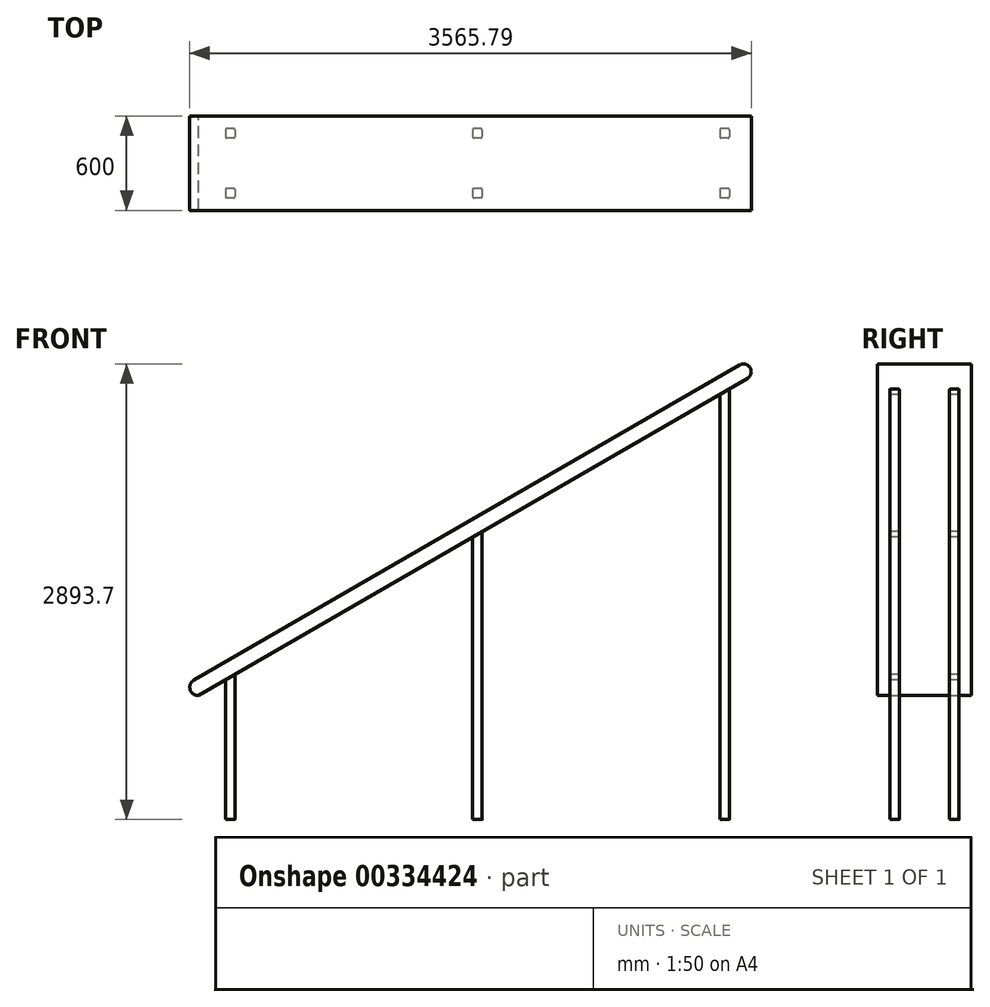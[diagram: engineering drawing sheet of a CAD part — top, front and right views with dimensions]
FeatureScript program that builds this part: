
annotation { "Feature Type Name" : "Feature", "Feature Type Description" : "" }
export const myFeature = defineFeature(function(context is Context, id is Id, definition is map)
    precondition{}
    {
        {
            var Q0;
            Q0=qCreatedBy(makeId("Front.planeOp"),FACE);
            var sketch = newSketch(context, id + "F0", { "sketchPlane" : qUnion([Q0])});
            skLineSegment(sketch, "E0.bottom", {"start": v(-3436.6, -2099.6) * mm, "end": v(50, -86.6) * mm});
            skLineSegment(sketch, "E0.top", {"start": v(-3464.1, -2000) * mm, "end": v(0, 0) * mm});
            skArc(sketch, "E1", {"start": v(-3464.1, -2000) * mm, "mid": v(-3488.86, -2060.43) * mm, "end": v(-3436.6, -2099.6) * mm});
            skArc(sketch, "E2", {"start": v(50, -86.6) * mm, "mid": v(68.3, -18.3) * mm, "end": v(0, 0) * mm});
            skLineSegment(sketch, "E3", {"start": v(25, -43.3) * mm, "end": v(-1405.55, -43.3) * mm, "construction": true});
            skSolve(sketch);
        }
        {
            var Q0;
            Q0 = qSketchRegion(id + "F0", true);
            extrude(context, id + "F1", {"entities" : qUnion([Q0]), "depth" : 600 * mm});
        }
        {
            var Q0;
            Q0=qCreatedBy(makeId("Top.planeOp"),FACE);
            cPlane(context, id + "F2", {"entities" : qUnion([Q0]), "cplaneType" : CPlaneType.OFFSET, "offset" : 2887 * mm, "oppositeDirection" : true, "width" : 150 * mm, "height" : 150 * mm});
        }
        {
            var Q0;
            Q0=qCreatedBy(id+"F2.planeOp",FACE);
            var sketch = newSketch(context, id + "F3", { "sketchPlane" : qUnion([Q0])});
            skLineSegment(sketch, "E4.bottom", {"start": v(-3212.1, -80) * mm, "end": v(-3256.1, -80) * mm});
            skLineSegment(sketch, "E4.top", {"start": v(-3212.1, -140) * mm, "end": v(-3256.1, -140) * mm});
            skLineSegment(sketch, "E4.left", {"start": v(-3204.1, -88) * mm, "end": v(-3204.1, -132) * mm});
            skLineSegment(sketch, "E4.right", {"start": v(-3264.1, -88) * mm, "end": v(-3264.1, -132) * mm});
            skPoint(sketch, "E4.middle", {"position": v(-3234.1, -110) * mm});
            skPoint(sketch, "E5.visualSharp", {"position": v(-3264.1, -140) * mm});
            skArc(sketch, "E5.filletArc", {"start": v(-3264.1, -132) * mm, "mid": v(-3261.76, -137.66) * mm, "end": v(-3256.1, -140) * mm});
            skPoint(sketch, "E6.visualSharp", {"position": v(-3204.1, -140) * mm});
            skArc(sketch, "E6.filletArc", {"start": v(-3212.1, -140) * mm, "mid": v(-3206.44, -137.66) * mm, "end": v(-3204.1, -132) * mm});
            skPoint(sketch, "E7.visualSharp", {"position": v(-3204.1, -80) * mm});
            skArc(sketch, "E7.filletArc", {"start": v(-3204.1, -88) * mm, "mid": v(-3206.44, -82.34) * mm, "end": v(-3212.1, -80) * mm});
            skPoint(sketch, "E8.visualSharp", {"position": v(-3264.1, -80) * mm});
            skArc(sketch, "E8.filletArc", {"start": v(-3256.1, -80) * mm, "mid": v(-3261.76, -82.34) * mm, "end": v(-3264.1, -88) * mm});
            skLineSegment(sketch, "E9", {"start": v(-3745.7, -300) * mm, "end": v(99.52, -300) * mm, "construction": true});
            skPoint(sketch, "E10.0.1.0", {"position": v(-3204.1, -460) * mm});
            skPoint(sketch, "E10.0.1.1", {"position": v(-3264.1, -460) * mm});
            skLineSegment(sketch, "E10.0.1.2", {"start": v(-3212.1, -460) * mm, "end": v(-3256.1, -460) * mm});
            skPoint(sketch, "E10.0.1.3", {"position": v(-3204.1, -520) * mm});
            skLineSegment(sketch, "E10.0.1.4", {"start": v(-3264.1, -468) * mm, "end": v(-3264.1, -512) * mm});
            skLineSegment(sketch, "E10.0.1.5", {"start": v(-3204.1, -468) * mm, "end": v(-3204.1, -512) * mm});
            skLineSegment(sketch, "E10.0.1.6", {"start": v(-3212.1, -520) * mm, "end": v(-3256.1, -520) * mm});
            skPoint(sketch, "E10.0.1.7", {"position": v(-3234.1, -490) * mm});
            skPoint(sketch, "E10.0.1.8", {"position": v(-3264.1, -520) * mm});
            skArc(sketch, "E10.0.1.9", {"start": v(-3204.1, -468) * mm, "mid": v(-3206.44, -462.34) * mm, "end": v(-3212.1, -460) * mm});
            skArc(sketch, "E10.0.1.10", {"start": v(-3256.1, -460) * mm, "mid": v(-3261.76, -462.34) * mm, "end": v(-3264.1, -468) * mm});
            skArc(sketch, "E10.0.1.11", {"start": v(-3264.1, -512) * mm, "mid": v(-3261.76, -517.66) * mm, "end": v(-3256.1, -520) * mm});
            skArc(sketch, "E10.0.1.12", {"start": v(-3212.1, -520) * mm, "mid": v(-3206.44, -517.66) * mm, "end": v(-3204.1, -512) * mm});
            skPoint(sketch, "E10.1.0.0", {"position": v(-1634.1, -80) * mm});
            skPoint(sketch, "E10.1.0.1", {"position": v(-1694.1, -80) * mm});
            skLineSegment(sketch, "E10.1.0.2", {"start": v(-1642.1, -80) * mm, "end": v(-1686.1, -80) * mm});
            skPoint(sketch, "E10.1.0.3", {"position": v(-1634.1, -140) * mm});
            skLineSegment(sketch, "E10.1.0.4", {"start": v(-1694.1, -88) * mm, "end": v(-1694.1, -132) * mm});
            skLineSegment(sketch, "E10.1.0.5", {"start": v(-1634.1, -88) * mm, "end": v(-1634.1, -132) * mm});
            skLineSegment(sketch, "E10.1.0.6", {"start": v(-1642.1, -140) * mm, "end": v(-1686.1, -140) * mm});
            skPoint(sketch, "E10.1.0.7", {"position": v(-1664.1, -110) * mm});
            skPoint(sketch, "E10.1.0.8", {"position": v(-1694.1, -140) * mm});
            skArc(sketch, "E10.1.0.9", {"start": v(-1634.1, -88) * mm, "mid": v(-1636.44, -82.34) * mm, "end": v(-1642.1, -80) * mm});
            skArc(sketch, "E10.1.0.10", {"start": v(-1686.1, -80) * mm, "mid": v(-1691.76, -82.34) * mm, "end": v(-1694.1, -88) * mm});
            skArc(sketch, "E10.1.0.11", {"start": v(-1694.1, -132) * mm, "mid": v(-1691.76, -137.66) * mm, "end": v(-1686.1, -140) * mm});
            skArc(sketch, "E10.1.0.12", {"start": v(-1642.1, -140) * mm, "mid": v(-1636.44, -137.66) * mm, "end": v(-1634.1, -132) * mm});
            skPoint(sketch, "E10.1.1.0", {"position": v(-1634.1, -460) * mm});
            skPoint(sketch, "E10.1.1.1", {"position": v(-1694.1, -460) * mm});
            skLineSegment(sketch, "E10.1.1.2", {"start": v(-1642.1, -460) * mm, "end": v(-1686.1, -460) * mm});
            skPoint(sketch, "E10.1.1.3", {"position": v(-1634.1, -520) * mm});
            skLineSegment(sketch, "E10.1.1.4", {"start": v(-1694.1, -468) * mm, "end": v(-1694.1, -512) * mm});
            skLineSegment(sketch, "E10.1.1.5", {"start": v(-1634.1, -468) * mm, "end": v(-1634.1, -512) * mm});
            skLineSegment(sketch, "E10.1.1.6", {"start": v(-1642.1, -520) * mm, "end": v(-1686.1, -520) * mm});
            skPoint(sketch, "E10.1.1.7", {"position": v(-1664.1, -490) * mm});
            skPoint(sketch, "E10.1.1.8", {"position": v(-1694.1, -520) * mm});
            skArc(sketch, "E10.1.1.9", {"start": v(-1634.1, -468) * mm, "mid": v(-1636.44, -462.34) * mm, "end": v(-1642.1, -460) * mm});
            skArc(sketch, "E10.1.1.10", {"start": v(-1686.1, -460) * mm, "mid": v(-1691.76, -462.34) * mm, "end": v(-1694.1, -468) * mm});
            skArc(sketch, "E10.1.1.11", {"start": v(-1694.1, -512) * mm, "mid": v(-1691.76, -517.66) * mm, "end": v(-1686.1, -520) * mm});
            skArc(sketch, "E10.1.1.12", {"start": v(-1642.1, -520) * mm, "mid": v(-1636.44, -517.66) * mm, "end": v(-1634.1, -512) * mm});
            skPoint(sketch, "E10.2.0.0", {"position": v(-64.1, -80) * mm});
            skPoint(sketch, "E10.2.0.1", {"position": v(-124.1, -80) * mm});
            skLineSegment(sketch, "E10.2.0.2", {"start": v(-72.1, -80) * mm, "end": v(-116.1, -80) * mm});
            skPoint(sketch, "E10.2.0.3", {"position": v(-64.1, -140) * mm});
            skLineSegment(sketch, "E10.2.0.4", {"start": v(-124.1, -88) * mm, "end": v(-124.1, -132) * mm});
            skLineSegment(sketch, "E10.2.0.5", {"start": v(-64.1, -88) * mm, "end": v(-64.1, -132) * mm});
            skLineSegment(sketch, "E10.2.0.6", {"start": v(-72.1, -140) * mm, "end": v(-116.1, -140) * mm});
            skPoint(sketch, "E10.2.0.7", {"position": v(-94.1, -110) * mm});
            skPoint(sketch, "E10.2.0.8", {"position": v(-124.1, -140) * mm});
            skArc(sketch, "E10.2.0.9", {"start": v(-64.1, -88) * mm, "mid": v(-66.44, -82.34) * mm, "end": v(-72.1, -80) * mm});
            skArc(sketch, "E10.2.0.10", {"start": v(-116.1, -80) * mm, "mid": v(-121.76, -82.34) * mm, "end": v(-124.1, -88) * mm});
            skArc(sketch, "E10.2.0.11", {"start": v(-124.1, -132) * mm, "mid": v(-121.76, -137.66) * mm, "end": v(-116.1, -140) * mm});
            skArc(sketch, "E10.2.0.12", {"start": v(-72.1, -140) * mm, "mid": v(-66.44, -137.66) * mm, "end": v(-64.1, -132) * mm});
            skPoint(sketch, "E10.2.1.0", {"position": v(-64.1, -460) * mm});
            skPoint(sketch, "E10.2.1.1", {"position": v(-124.1, -460) * mm});
            skLineSegment(sketch, "E10.2.1.2", {"start": v(-72.1, -460) * mm, "end": v(-116.1, -460) * mm});
            skPoint(sketch, "E10.2.1.3", {"position": v(-64.1, -520) * mm});
            skLineSegment(sketch, "E10.2.1.4", {"start": v(-124.1, -468) * mm, "end": v(-124.1, -512) * mm});
            skLineSegment(sketch, "E10.2.1.5", {"start": v(-64.1, -468) * mm, "end": v(-64.1, -512) * mm});
            skLineSegment(sketch, "E10.2.1.6", {"start": v(-72.1, -520) * mm, "end": v(-116.1, -520) * mm});
            skPoint(sketch, "E10.2.1.7", {"position": v(-94.1, -490) * mm});
            skPoint(sketch, "E10.2.1.8", {"position": v(-124.1, -520) * mm});
            skArc(sketch, "E10.2.1.9", {"start": v(-64.1, -468) * mm, "mid": v(-66.44, -462.34) * mm, "end": v(-72.1, -460) * mm});
            skArc(sketch, "E10.2.1.10", {"start": v(-116.1, -460) * mm, "mid": v(-121.76, -462.34) * mm, "end": v(-124.1, -468) * mm});
            skArc(sketch, "E10.2.1.11", {"start": v(-124.1, -512) * mm, "mid": v(-121.76, -517.66) * mm, "end": v(-116.1, -520) * mm});
            skArc(sketch, "E10.2.1.12", {"start": v(-72.1, -520) * mm, "mid": v(-66.44, -517.66) * mm, "end": v(-64.1, -512) * mm});
            skLineSegment(sketch, "E10.direction1", {"start": v(-3264.1, -140) * mm, "end": v(-1694.1, -140) * mm, "construction": true});
            skLineSegment(sketch, "E10.direction2", {"start": v(-3264.1, -140) * mm, "end": v(-3264.1, -520) * mm, "construction": true});
            skSolve(sketch);
        }
        {
            var Q0;
            Q0 = qSketchRegion(id + "F3", true);
            var Q1;
            Q1=makeQuery(id+"F1.opExtrude","SWEPT_FACE",FACE,{"disambiguationData":[OSD([sQuery(id+"F0.wireOp",EDGE,"E0.bottom")])]});
            extrude(context, id + "F4", {"entities" : qUnion([Q0]), "operationType" : NewBodyOperationType.ADD, "endBound" : BoundingType.UP_TO_SURFACE, "endBoundEntityFace" : qUnion([Q1]), "depth" : 25 * mm});
        }
    });
